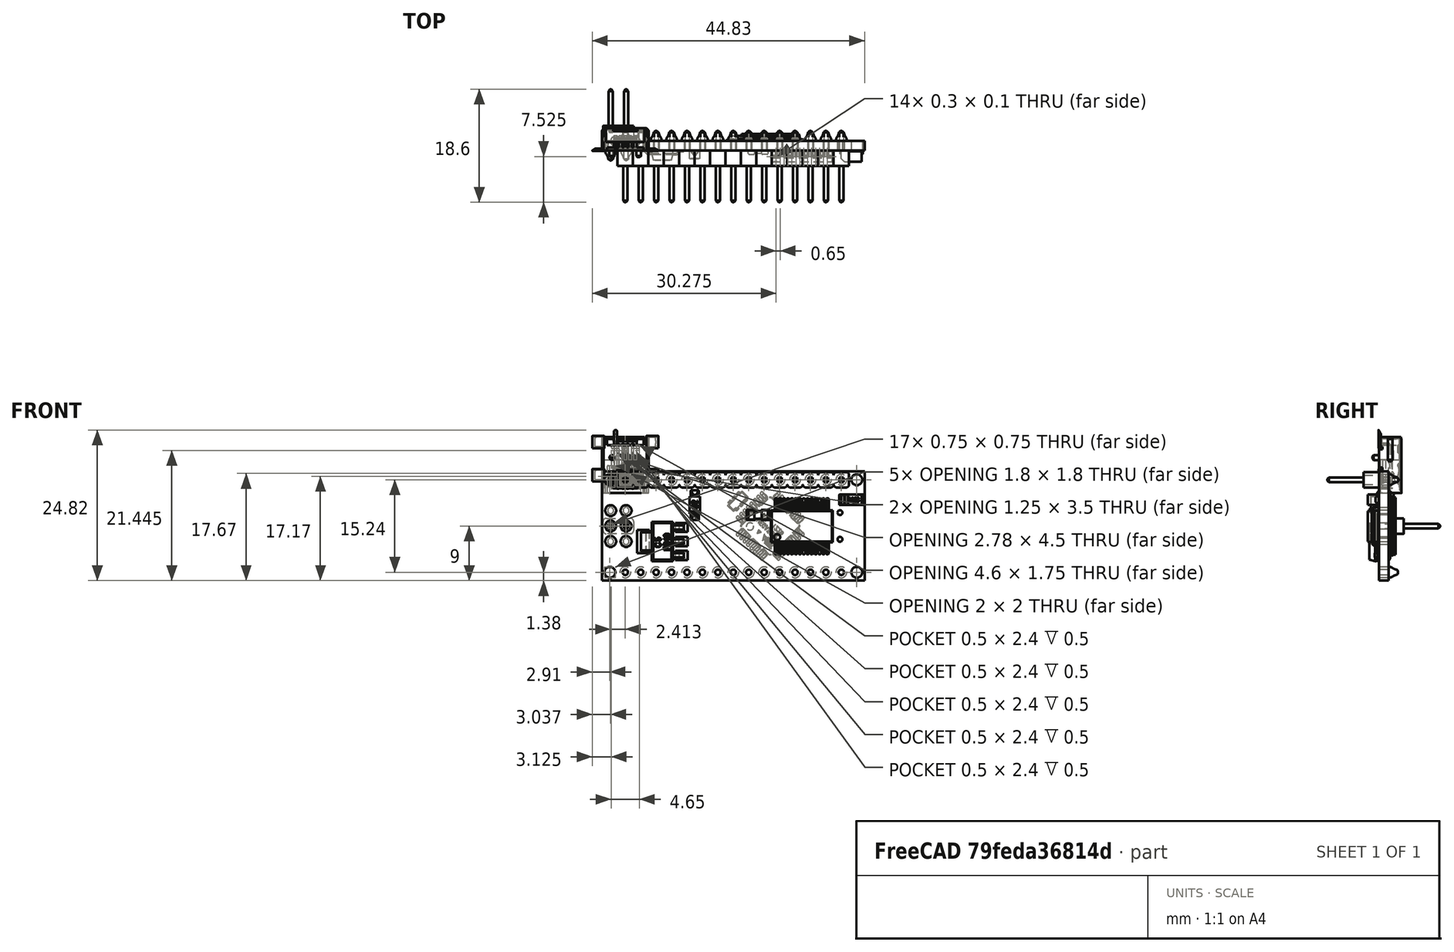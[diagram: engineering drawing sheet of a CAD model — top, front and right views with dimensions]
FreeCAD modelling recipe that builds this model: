
FCSTD DOCUMENT  (FreeCAD 2022.709R28846 (Git))
Label: footprint_Arduino_Nano_V2
License: Other
objects: Part::Feature×37, App::Link×15, Part::Compound2×3, App::Part×3
note: 37 computed .brp shape members not serialized (recipe doc carries the construction recipe); baked Part::Feature solids carry a one-line shape summary decoded from their .brp

FEATURE [Part::Feature] Solid  label="nano-board"
  TreeRank = 7
  shape: bbox 43.2 x 4.77 x 18 mm, 378 faces (baked)
FEATURE [Part::Feature] Solid001  label="2pin_header__02"
  Placement = pos=(-1.143,1.6,-7.62) rot=(0,0,1;0rad)
  TreeRank = 8
  shape: bbox 5 x 11.75 x 2.54 mm, 46 faces (baked)
FEATURE [App::Link] Link  label="NAUO3"
  AutoLinkLabel = true
  AutoPlacement = true
  LinkPlacement = pos=(-1.143,1.6,-5.08) rot=(0,0,1;0rad)
  LinkedObject = -> Solid001
  Placement = pos=(-1.143,1.6,-5.08) rot=(0,0,1;0rad)
  ShowElement = false
  SyncGroupVisibility = false
  TreeRank = 9
  _LinkVersion = 1
FEATURE [App::Link] Link001  label="NAUO4"
  AutoLinkLabel = true
  AutoPlacement = true
  LinkPlacement = pos=(-1.143,1.6,-10.16) rot=(0,0,1;0rad)
  LinkedObject = -> Solid001
  Placement = pos=(-1.143,1.6,-10.16) rot=(0,0,1;0rad)
  ShowElement = false
  SyncGroupVisibility = false
  TreeRank = 10
  _LinkVersion = 1
FEATURE [Part::Feature] Solid002  label="15pin_header__"
  Placement = pos=(0,0,0) rot=(0.707107,0,0.707107;3.14159rad)
  TreeRank = 11
  shape: bbox 38.1 x 11.75 x 2.54 mm, 364 faces (baked)
FEATURE [App::Link] Link002  label="NAUO6"
  AutoLinkLabel = true
  AutoPlacement = true
  LinkPlacement = pos=(-2.5e-15,0,-15.24) rot=(0.707107,0,0.707107;3.14159rad)
  LinkedObject = -> Solid002
  Placement = pos=(-2.5e-15,0,-15.24) rot=(0.707107,0,0.707107;3.14159rad)
  ShowElement = false
  SyncGroupVisibility = false
  TreeRank = 12
  _LinkVersion = 1
FEATURE [Part::Feature] Solid003  label="atmega328"
  Placement = pos=(23.85,1.75,-7.62) rot=(0,1,0;3.92699rad)
  TreeRank = 13
  shape: bbox 11.25 x 1.2 x 11.25 mm, 1867 faces (baked)
FEATURE [Part::Feature] Solid004  label="ftdi FT232rl"
  Placement = pos=(29.05,1e-16,-7.67) rot=(-0.707107,0,0.707107;3.14159rad)
  TreeRank = 14
  shape: bbox 10.2 x 1.9 x 9.287 mm, 717 faces (baked)
FEATURE [Part::Feature] Solid005  label="smt_resistor222"
  Placement = pos=(21.86,0,-5.8) rot=(-0.707107,0,0.707107;3.14159rad)
  TreeRank = 23
  shape: bbox 3.8 x 0.6 x 1.813 mm, 74 faces (baked)
FEATURE [App::Link] Link003  label="NAUO10"
  AutoLinkLabel = true
  AutoPlacement = true
  LinkPlacement = pos=(21.86,0,-9) rot=(-0.707107,0,0.707107;3.14159rad)
  LinkedObject = -> Solid005
  Placement = pos=(21.86,0,-9) rot=(-0.707107,0,0.707107;3.14159rad)
  ShowElement = false
  SyncGroupVisibility = false
  TreeRank = 24
  _LinkVersion = 1
FEATURE [App::Link] Link004  label="NAUO11"
  AutoLinkLabel = true
  AutoPlacement = true
  LinkPlacement = pos=(36.75,0,-7.6) rot=(-0.707107,0,0.707107;3.14159rad)
  LinkedObject = -> Solid005
  Placement = pos=(36.75,0,-7.6) rot=(-0.707107,0,0.707107;3.14159rad)
  ShowElement = false
  SyncGroupVisibility = false
  TreeRank = 25
  _LinkVersion = 1
FEATURE [App::Link] Link005  label="NAUO12"
  AutoLinkLabel = true
  AutoPlacement = true
  LinkPlacement = pos=(36.75,0,-12) rot=(-0.707107,0,0.707107;3.14159rad)
  LinkedObject = -> Solid005
  Placement = pos=(36.75,0,-12) rot=(-0.707107,0,0.707107;3.14159rad)
  ShowElement = false
  SyncGroupVisibility = false
  TreeRank = 26
  _LinkVersion = 1
FEATURE [App::Link] Link006  label="NAUO13"
  AutoLinkLabel = true
  AutoPlacement = true
  LinkPlacement = pos=(8.2,0,-2.6) rot=(-0.707107,0,0.707107;3.14159rad)
  LinkedObject = -> Solid005
  Placement = pos=(8.2,0,-2.6) rot=(-0.707107,0,0.707107;3.14159rad)
  ShowElement = false
  SyncGroupVisibility = false
  TreeRank = 27
  _LinkVersion = 1
FEATURE [Part::Feature] Solid006
  TreeRank = 28
  shape: bbox 4.438 x 0.5452 x 2.138 mm, 51 faces (baked)
FEATURE [Part::Feature] Solid007
  TreeRank = 29
  shape: bbox 1.4 x 0.5 x 1.2 mm, 6 faces (baked)
FEATURE [Part::Compound2] Compound  label="led"
  Links = -> [Solid006,Solid007]
  Placement = pos=(10.4,1.6,-2.8) rot=(0,0,1;0rad)
  TreeRank = 30
FEATURE [App::Link] Link007  label="NAUO15"
  AutoLinkLabel = true
  AutoPlacement = true
  LinkPlacement = pos=(10.4,1.6,-5.55) rot=(0,0,1;0rad)
  LinkedObject = -> Compound
  Placement = pos=(10.4,1.6,-5.55) rot=(0,0,1;0rad)
  ShowElement = false
  SyncGroupVisibility = false
  TreeRank = 37
  _LinkVersion = 1
FEATURE [App::Link] Link008  label="NAUO16"
  AutoLinkLabel = true
  AutoPlacement = true
  LinkPlacement = pos=(10.4,1.6,-12.5) rot=(0,0,1;0rad)
  LinkedObject = -> Compound
  Placement = pos=(10.4,1.6,-12.5) rot=(0,0,1;0rad)
  ShowElement = false
  SyncGroupVisibility = false
  TreeRank = 38
  _LinkVersion = 1
FEATURE [App::Link] Link009  label="NAUO17"
  AutoLinkLabel = true
  AutoPlacement = true
  LinkPlacement = pos=(10.4,1.6,-9.05) rot=(0,0,1;0rad)
  LinkedObject = -> Compound
  Placement = pos=(10.4,1.6,-9.05) rot=(0,0,1;0rad)
  ShowElement = false
  SyncGroupVisibility = false
  TreeRank = 39
  _LinkVersion = 1
FEATURE [Part::Feature] Solid008  label="16mhz crystal - measured"
  Placement = pos=(18.5113,1.6,-3.55414) rot=(0,-1,0;0.785398rad)
  TreeRank = 40
  shape: bbox 3.394 x 0.8 x 3.394 mm, 71 faces (baked)
FEATURE [Part::Feature] Solid009  label="MINIUSBSHELL"
  TreeRank = 41
  shape: bbox 11.03 x 3.822 x 9.475 mm, 243 faces (baked)
FEATURE [Part::Feature] Solid010  label="MINIUSBCORE"
  Placement = pos=(0,0,6.7) rot=(0,1,0;3.14159rad)
  TreeRank = 42
  shape: bbox 7.7 x 4.5 x 8.2 mm, 127 faces (baked)
FEATURE [Part::Feature] Solid011  label="MINI USB CONTACT"
  Placement = pos=(-1.6,0,5.7) rot=(0,1,0;3.14159rad)
  TreeRank = 58
  shape: bbox 0.5011 x 2.551 x 9.423 mm, 31 faces (baked)
FEATURE [App::Link] Link010  label="NAUO32"
  AutoLinkLabel = true
  AutoPlacement = true
  LinkPlacement = pos=(-0.8,0,5.7) rot=(0,1,0;3.14159rad)
  LinkedObject = -> Solid011
  Placement = pos=(-0.8,0,5.7) rot=(0,1,0;3.14159rad)
  ShowElement = false
  SyncGroupVisibility = false
  TreeRank = 59
  _LinkVersion = 1
FEATURE [App::Link] Link011  label="NAUO33"
  AutoLinkLabel = true
  AutoPlacement = true
  LinkPlacement = pos=(0,0,5.7) rot=(0,1,0;3.14159rad)
  LinkedObject = -> Solid011
  Placement = pos=(0,0,5.7) rot=(0,1,0;3.14159rad)
  ShowElement = false
  SyncGroupVisibility = false
  TreeRank = 60
  _LinkVersion = 1
FEATURE [App::Link] Link012  label="NAUO34"
  AutoLinkLabel = true
  AutoPlacement = true
  LinkPlacement = pos=(0.8,0,5.7) rot=(0,1,0;3.14159rad)
  LinkedObject = -> Solid011
  Placement = pos=(0.8,0,5.7) rot=(0,1,0;3.14159rad)
  ShowElement = false
  SyncGroupVisibility = false
  TreeRank = 61
  _LinkVersion = 1
FEATURE [App::Link] Link013  label="NAUO35"
  AutoLinkLabel = true
  AutoPlacement = true
  LinkPlacement = pos=(1.6,0,5.7) rot=(0,1,0;3.14159rad)
  LinkedObject = -> Solid011
  Placement = pos=(1.6,0,5.7) rot=(0,1,0;3.14159rad)
  ShowElement = false
  SyncGroupVisibility = false
  TreeRank = 62
  _LinkVersion = 1
FEATURE [App::Part] Part  label="MINIUSB - MEASURED"
  ClaimAllChildren = false
  ExportMode = 1
  Group = -> [Solid009,Solid010,Solid011,Link010,Link011,Link012,Link013]
  Origin = -> Origin
  Placement = pos=(38.98,1.65,-7.62) rot=(0,-1,0;1.5708rad)
  TreeRank = 64
  _ExportChildren = -> [Solid009,Solid010,Solid011,Link010,Link011,Link012,Link013]
  _GroupVersion = 1
FEATURE [Part::Feature] Solid012  label="cap106C"
  Placement = pos=(37.2,-1e-16,-3.3) rot=(0.707107,0,0.707107;3.14159rad)
  TreeRank = 65
  shape: bbox 4.001 x 1.811 x 1.701 mm, 124 faces (baked)
FEATURE [App::Link] Link014  label="NAUO21"
  AutoLinkLabel = true
  AutoPlacement = true
  LinkPlacement = pos=(7.9,-7e-16,-5.6) rot=(-0.707107,0,0.707107;3.14159rad)
  LinkedObject = -> Solid012
  Placement = pos=(7.9,-7e-16,-5.6) rot=(-0.707107,0,0.707107;3.14159rad)
  ShowElement = false
  SyncGroupVisibility = false
  TreeRank = 66
  _LinkVersion = 1
FEATURE [Part::Feature] Solid013  label="reset core"
  TreeRank = 67
  shape: bbox 5.2 x 2.15 x 2.8 mm, 77 faces (baked)
FEATURE [Part::Feature] Solid014  label="reset shell"
  Placement = pos=(0,1.65,0) rot=(0,-1,0;1.5708rad)
  TreeRank = 68
  shape: bbox 4 x 1.65 x 3 mm, 100 faces (baked)
FEATURE [App::Part] Part001  label="reset button"
  ClaimAllChildren = false
  ExportMode = 1
  Group = -> [Solid013,Solid014]
  Origin = -> Origin001
  Placement = pos=(15.25,1.6,-8.05) rot=(0,1,0;1.5708rad)
  TreeRank = 70
  _ExportChildren = -> [Solid013,Solid014]
  _GroupVersion = 1
FEATURE [Part::Feature] Solid015  label="nano - reg"
  Placement = pos=(6.1,0,-10.16) rot=(-0.707107,0,0.707107;3.14159rad)
  TreeRank = 71
  shape: bbox 8.3 x 1.689 x 6.5 mm, 198 faces (baked)
FEATURE [Part::Feature] Solid016  label="NANO DIODE"
  Placement = pos=(11.43,0,-4.2) rot=(0.707107,0,0.707107;3.14159rad)
  TreeRank = 72
  shape: bbox 1.7 x 1.384 x 4.916 mm, 85 faces (baked)
FEATURE [Part::Feature] Solid017
  TreeRank = 84
  shape: bbox 3.2 x 0.3 x 1.3 mm, 21 faces (baked)
FEATURE [Part::Feature] Solid018
  TreeRank = 85
  shape: bbox 3.2 x 0.455 x 1.5 mm, 147 faces (baked)
FEATURE [Part::Feature] Solid019
  TreeRank = 86
  shape: bbox 0.4001 x 0.4736 x 0.9095 mm, 15 faces (baked)
FEATURE [Part::Feature] Solid020
  TreeRank = 87
  shape: bbox 0.4001 x 0.4736 x 0.9095 mm, 15 faces (baked)
FEATURE [Part::Feature] Solid021
  TreeRank = 88
  shape: bbox 0.4001 x 0.4736 x 0.9095 mm, 15 faces (baked)
FEATURE [Part::Feature] Solid022
  TreeRank = 89
  shape: bbox 0.4001 x 0.4736 x 0.9095 mm, 15 faces (baked)
FEATURE [Part::Feature] Solid023
  TreeRank = 90
  shape: bbox 0.4001 x 0.4736 x 0.9095 mm, 15 faces (baked)
FEATURE [Part::Feature] Solid024
  TreeRank = 91
  shape: bbox 0.4001 x 0.4736 x 0.9095 mm, 15 faces (baked)
FEATURE [Part::Feature] Solid025
  TreeRank = 92
  shape: bbox 0.4001 x 0.4736 x 0.9095 mm, 15 faces (baked)
FEATURE [Part::Feature] Solid026
  TreeRank = 93
  shape: bbox 0.4001 x 0.4736 x 0.9095 mm, 15 faces (baked)
FEATURE [Part::Compound2] Compound001  label="189 RESISTOR PACK"
  Links = -> [Solid017,Solid018,Solid019,Solid020,Solid021,Solid022,Solid023,Solid024,Solid025,Solid026]
  Placement = pos=(15.75,0,-10.85) rot=(0.707107,0,0.707107;3.14159rad)
  TreeRank = 94
FEATURE [Part::Feature] Solid027
  TreeRank = 106
  shape: bbox 3.2 x 0.3 x 1.3 mm, 21 faces (baked)
FEATURE [Part::Feature] Solid028
  TreeRank = 107
  shape: bbox 3.2 x 0.455 x 1.5 mm, 136 faces (baked)
FEATURE [Part::Feature] Solid029
  TreeRank = 108
  shape: bbox 0.4001 x 0.4736 x 0.9095 mm, 15 faces (baked)
FEATURE [Part::Feature] Solid030
  TreeRank = 109
  shape: bbox 0.4001 x 0.4736 x 0.9095 mm, 15 faces (baked)
FEATURE [Part::Feature] Solid031
  TreeRank = 110
  shape: bbox 0.4001 x 0.4736 x 0.9095 mm, 15 faces (baked)
FEATURE [Part::Feature] Solid032
  TreeRank = 111
  shape: bbox 0.4001 x 0.4736 x 0.9095 mm, 15 faces (baked)
FEATURE [Part::Feature] Solid033
  TreeRank = 112
  shape: bbox 0.4001 x 0.4736 x 0.9095 mm, 15 faces (baked)
FEATURE [Part::Feature] Solid034
  TreeRank = 113
  shape: bbox 0.4001 x 0.4736 x 0.9095 mm, 15 faces (baked)
FEATURE [Part::Feature] Solid035
  TreeRank = 114
  shape: bbox 0.4001 x 0.4736 x 0.9095 mm, 15 faces (baked)
FEATURE [Part::Feature] Solid036
  TreeRank = 115
  shape: bbox 0.4001 x 0.4736 x 0.9095 mm, 15 faces (baked)
FEATURE [Part::Compound2] Compound002  label="102 RESISTOR PACK"
  Links = -> [Solid027,Solid028,Solid029,Solid030,Solid031,Solid032,Solid033,Solid034,Solid035,Solid036]
  Placement = pos=(15.75,0,-5.2) rot=(0.707107,0,0.707107;3.14159rad)
  TreeRank = 116
FEATURE [App::Part] Part002  label="arduino nano"
  ClaimAllChildren = false
  ExportMode = 1
  Group = -> [Solid,Solid001,Link,Link001,Solid002,Link002,Solid003,Solid004,Solid005,Link003,Link004,Link005,Link006,Compound,Link007,Link008,Link009,Solid008,Part,Solid012,Link014,Part001,Solid015,Solid016,Compound001,Compound002,Solid007,Solid006,Solid020,Solid022,Solid025,Solid026,Solid019,Solid017,Solid023,Solid024,Solid018,Solid021,Solid030,Solid027,Solid031,Solid032,Solid029,Solid028,Solid034,Solid036,+2 more]
  Origin = -> Origin002
  Placement = pos=(-7.606,-2.54,2.54) rot=(-0.57735,0.57735,0.57735;4.18879rad)
  TreeRank = 119
  _ExportChildren = -> [Solid,Solid001,Link,Link001,Solid002,Link002,Solid003,Solid004,Solid005,Link003,Link004,Link005,Link006,Compound,Link007,Link008,Link009,Solid008,Part,Solid012,Link014,Part001,Solid015,Solid016,Compound001,Compound002]
  _GroupVersion = 1
